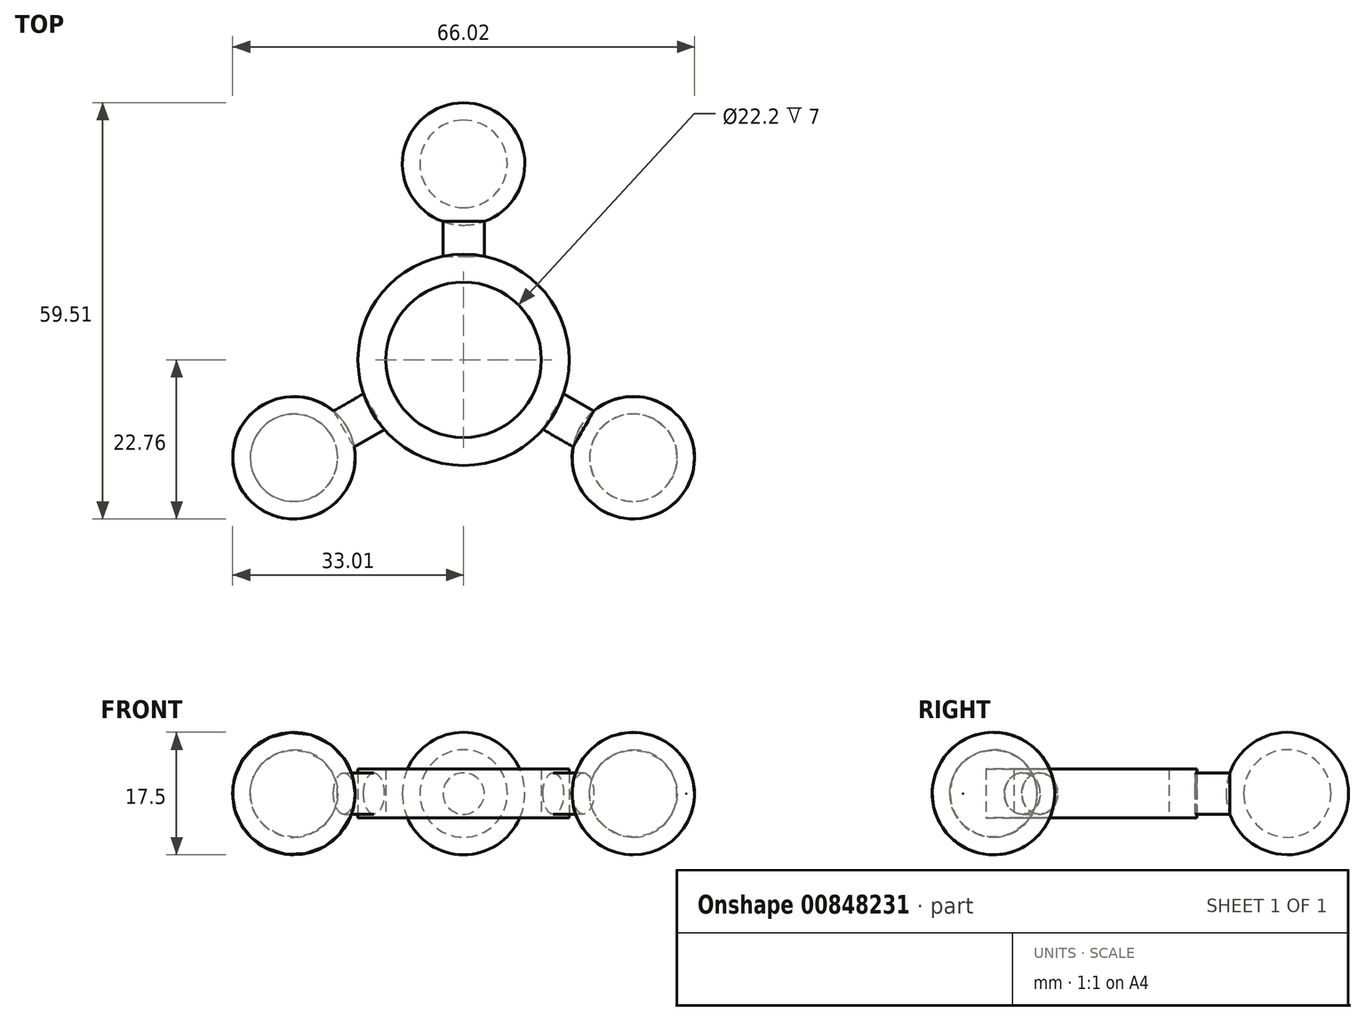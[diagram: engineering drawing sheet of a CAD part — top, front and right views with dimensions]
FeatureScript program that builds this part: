
annotation { "Feature Type Name" : "Feature", "Feature Type Description" : "" }
export const myFeature = defineFeature(function(context is Context, id is Id, definition is map)
    precondition{}
    {
        {
            var Q0;
            Q0=qCreatedBy(makeId("Top.planeOp"),FACE);
            var sketch = newSketch(context, id + "F0", { "sketchPlane" : qUnion([Q0])});
            skCircle(sketch, "E0", {"center": v(0, 0) * mm, "radius": 11.1 * mm});
            skArc(sketch, "E1", {"start": v(0, 21.75) * mm, "mid": v(6.25, 28) * mm, "end": v(0, 34.25) * mm});
            skArc(sketch, "E2", {"start": v(0, 19.25) * mm, "mid": v(8.75, 28) * mm, "end": v(0, 36.75) * mm});
            skLineSegment(sketch, "E3", {"start": v(-3, 14.8) * mm, "end": v(-3, 10.69) * mm});
            skLineSegment(sketch, "E4.MirrorCS", {"start": v(2.95, 19.77) * mm, "end": v(2.95, 10.7) * mm});
            skArc(sketch, "E5.1.0", {"start": v(-16.68, -9.63) * mm, "mid": v(-28.63, -6.43) * mm, "end": v(-31.83, -18.38) * mm});
            skArc(sketch, "E5.2.0", {"start": v(16.68, -9.63) * mm, "mid": v(19.88, -21.58) * mm, "end": v(31.83, -18.38) * mm});
            skLineSegment(sketch, "E6.1.0", {"start": v(-18.6, -7.33) * mm, "end": v(-10.75, -2.8) * mm});
            skLineSegment(sketch, "E6.1.1", {"start": v(-11.32, -10) * mm, "end": v(-7.76, -7.95) * mm});
            skArc(sketch, "E6.1.2", {"start": v(-18.84, -10.88) * mm, "mid": v(-27.38, -8.6) * mm, "end": v(-29.67, -17.13) * mm});
            skLineSegment(sketch, "E6.2.0", {"start": v(15.64, -12.45) * mm, "end": v(7.8, -7.91) * mm});
            skLineSegment(sketch, "E6.2.1", {"start": v(14.31, -4.8) * mm, "end": v(10.76, -2.75) * mm});
            skArc(sketch, "E6.2.2", {"start": v(18.84, -10.88) * mm, "mid": v(21.13, -19.42) * mm, "end": v(29.67, -17.13) * mm});
            skCircle(sketch, "E7", {"center": v(0, 0) * mm, "radius": 15.1 * mm});
            skLineSegment(sketch, "E8", {"start": v(0, 0) * mm, "end": v(0, 50.7) * mm, "construction": true});
            skLineSegment(sketch, "E9.1.0", {"start": v(0, 0) * mm, "end": v(-43.9, -25.35) * mm, "construction": true});
            skLineSegment(sketch, "E9.2.0", {"start": v(0, 0) * mm, "end": v(43.9, -25.35) * mm, "construction": true});
            skLineSegment(sketch, "E10", {"start": v(-31.83, -18.38) * mm, "end": v(-29.67, -17.13) * mm});
            skLineSegment(sketch, "E11", {"start": v(-18.84, -10.88) * mm, "end": v(-16.68, -9.63) * mm});
            skLineSegment(sketch, "E12", {"start": v(16.68, -9.63) * mm, "end": v(18.84, -10.88) * mm});
            skLineSegment(sketch, "E13", {"start": v(29.67, -17.13) * mm, "end": v(31.83, -18.38) * mm});
            skLineSegment(sketch, "E14", {"start": v(0, 19.25) * mm, "end": v(0, 21.75) * mm});
            skLineSegment(sketch, "E15", {"start": v(0, 34.25) * mm, "end": v(0, 36.75) * mm});
            skPoint(sketch, "E16.orphan", {"position": v(-3, 19.78) * mm});
            skPoint(sketch, "E17.orphan", {"position": v(18.63, -7.3) * mm});
            skPoint(sketch, "E18.orphan", {"position": v(-15.64, -12.5) * mm});
            skLineSegment(sketch, "E19", {"start": v(0, 19.25) * mm, "end": v(0, 15.1) * mm});
            skLineSegment(sketch, "E20", {"start": v(16.68, -9.63) * mm, "end": v(13.08, -7.55) * mm});
            skLineSegment(sketch, "E21", {"start": v(-16.68, -9.63) * mm, "end": v(-13.08, -7.55) * mm});
            skSolve(sketch);
        }
        {
            var Q0;
            {var subQ0=sQuery(id+"F0.wireOp",EDGE,"E3");var subQ1=sQuery(id+"F0.wireOp",EDGE,"E0");var subQ2=makeQuery(id+"F0.imprint","INTERSECT",VERTEX,{"derivedFrom":[subQ1,subQ0]});Q0=makeQuery(id+"F0.imprint","IMPRINT",FACE,{"disambiguationData":[TD([[makeQuery(id+"F0.imprint","IMPRINT",EDGE,{"disambiguationData":[TD([[subQ2,-1.0]])],"derivedFrom":subQ1}),-1.0]])]});}
            var Q1;
            {var subQ0=sQuery(id+"F0.wireOp",EDGE,"E6.1.1");var subQ1=sQuery(id+"F0.wireOp",EDGE,"E0");var subQ2=makeQuery(id+"F0.imprint","INTERSECT",VERTEX,{"derivedFrom":[subQ1,subQ0]});Q1=makeQuery(id+"F0.imprint","IMPRINT",FACE,{"disambiguationData":[TD([[makeQuery(id+"F0.imprint","IMPRINT",EDGE,{"disambiguationData":[TD([[subQ2,-1.0]])],"derivedFrom":subQ1}),-1.0]])]});}
            var Q2;
            {var subQ0=sQuery(id+"F0.wireOp",EDGE,"E4.MirrorCS");var subQ1=sQuery(id+"F0.wireOp",EDGE,"E0");var subQ2=makeQuery(id+"F0.imprint","INTERSECT",VERTEX,{"derivedFrom":[subQ1,subQ0]});Q2=makeQuery(id+"F0.imprint","IMPRINT",FACE,{"disambiguationData":[TD([[makeQuery(id+"F0.imprint","IMPRINT",EDGE,{"disambiguationData":[TD([[subQ2,1.0]])],"derivedFrom":subQ1}),-1.0]])]});}
            var Q3;
            {var subQ0=sQuery(id+"F0.wireOp",EDGE,"E3");var subQ1=sQuery(id+"F0.wireOp",EDGE,"E0");var subQ2=makeQuery(id+"F0.imprint","INTERSECT",VERTEX,{"derivedFrom":[subQ1,subQ0]});Q3=makeQuery(id+"F0.imprint","IMPRINT",FACE,{"disambiguationData":[TD([[makeQuery(id+"F0.imprint","IMPRINT",EDGE,{"disambiguationData":[TD([[subQ2,1.0]])],"derivedFrom":subQ1}),-1.0]])]});}
            var Q4;
            {var subQ0=sQuery(id+"F0.wireOp",EDGE,"E6.1.0");var subQ1=sQuery(id+"F0.wireOp",EDGE,"E0");var subQ2=makeQuery(id+"F0.imprint","INTERSECT",VERTEX,{"derivedFrom":[subQ1,subQ0]});Q4=makeQuery(id+"F0.imprint","IMPRINT",FACE,{"disambiguationData":[TD([[makeQuery(id+"F0.imprint","IMPRINT",EDGE,{"disambiguationData":[TD([[subQ2,-1.0]])],"derivedFrom":subQ1}),-1.0]])]});}
            var Q5;
            {var subQ0=sQuery(id+"F0.wireOp",EDGE,"E6.2.0");var subQ1=sQuery(id+"F0.wireOp",EDGE,"E0");var subQ2=makeQuery(id+"F0.imprint","INTERSECT",VERTEX,{"derivedFrom":[subQ1,subQ0]});Q5=makeQuery(id+"F0.imprint","IMPRINT",FACE,{"disambiguationData":[TD([[makeQuery(id+"F0.imprint","IMPRINT",EDGE,{"disambiguationData":[TD([[subQ2,-1.0]])],"derivedFrom":subQ1}),-1.0]])]});}
            extrude(context, id + "F1", {"entities" : qUnion([Q0, Q1, Q2, Q3, Q4, Q5]), "endBound" : BoundingType.SYMMETRIC, "depth" : 7 * mm, "offsetDistance" : 25 * mm});
        }
        {
            var Q0;
            Q0=makeQuery(id+"F0.imprint","IMPRINT",FACE,{"disambiguationData":[TD([[makeQuery(id+"F0.imprint","IMPRINT",EDGE,{"derivedFrom":sQuery(id+"F0.wireOp",EDGE,"E6.1.2")}),-1.0]])]});
            var Q1;
            Q1=sQuery(id+"F0.wireOp",EDGE,"E9.1.0");
            revolve(context, id + "F2", {"operationType" : NewBodyOperationType.ADD, "surfaceOperationType" : NewSurfaceOperationType.NEW, "entities" : qUnion([Q0]), "axis" : qUnion([Q1]), "revolveType" : RevolveType.FULL});
        }
        {
            var Q0;
            Q0=makeQuery(id+"F0.imprint","IMPRINT",FACE,{"disambiguationData":[TD([[makeQuery(id+"F0.imprint","IMPRINT",EDGE,{"derivedFrom":sQuery(id+"F0.wireOp",EDGE,"E6.2.2")}),-1.0]])]});
            var Q1;
            Q1=sQuery(id+"F0.wireOp",EDGE,"E9.2.0");
            revolve(context, id + "F3", {"operationType" : NewBodyOperationType.ADD, "surfaceOperationType" : NewSurfaceOperationType.NEW, "entities" : qUnion([Q0]), "axis" : qUnion([Q1]), "revolveType" : RevolveType.FULL});
        }
        {
            var Q0;
            Q0=makeQuery(id+"F0.imprint","IMPRINT",FACE,{"disambiguationData":[TD([[makeQuery(id+"F0.imprint","IMPRINT",EDGE,{"derivedFrom":sQuery(id+"F0.wireOp",EDGE,"E1")}),-1.0]])]});
            var Q1;
            Q1=sQuery(id+"F0.wireOp",EDGE,"E8");
            revolve(context, id + "F4", {"operationType" : NewBodyOperationType.ADD, "surfaceOperationType" : NewSurfaceOperationType.NEW, "entities" : qUnion([Q0]), "axis" : qUnion([Q1]), "revolveType" : RevolveType.FULL});
        }
        {
            var Q0;
            {var subQ0=sQuery(id+"F0.wireOp",EDGE,"E19");Q0=makeQuery(id+"F0.imprint","IMPRINT",FACE,{"disambiguationData":[TD([[makeQuery(id+"F0.imprint","IMPRINT",EDGE,{"derivedFrom":subQ0}),1.0]])]});}
            var Q1;
            Q1=sQuery(id+"F0.wireOp",EDGE,"E8");
            revolve(context, id + "F5", {"surfaceOperationType" : NewSurfaceOperationType.NEW, "entities" : qUnion([Q0]), "axis" : qUnion([Q1]), "revolveType" : RevolveType.FULL});
        }
        {
            var Q0;
            {var subQ0=sQuery(id+"F0.wireOp",EDGE,"E20");Q0=makeQuery(id+"F0.imprint","IMPRINT",FACE,{"disambiguationData":[TD([[makeQuery(id+"F0.imprint","IMPRINT",EDGE,{"derivedFrom":subQ0}),1.0]])]});}
            var Q1;
            Q1=sQuery(id+"F0.wireOp",EDGE,"E9.2.0");
            revolve(context, id + "F6", {"surfaceOperationType" : NewSurfaceOperationType.NEW, "entities" : qUnion([Q0]), "axis" : qUnion([Q1]), "revolveType" : RevolveType.FULL});
        }
        {
            var Q0;
            {var subQ0=sQuery(id+"F0.wireOp",EDGE,"E21");Q0=makeQuery(id+"F0.imprint","IMPRINT",FACE,{"disambiguationData":[TD([[makeQuery(id+"F0.imprint","IMPRINT",EDGE,{"derivedFrom":subQ0}),1.0]])]});}
            var Q1;
            Q1=sQuery(id+"F0.wireOp",EDGE,"E9.1.0");
            revolve(context, id + "F7", {"surfaceOperationType" : NewSurfaceOperationType.NEW, "entities" : qUnion([Q0]), "axis" : qUnion([Q1]), "revolveType" : RevolveType.FULL});
        }
    });
